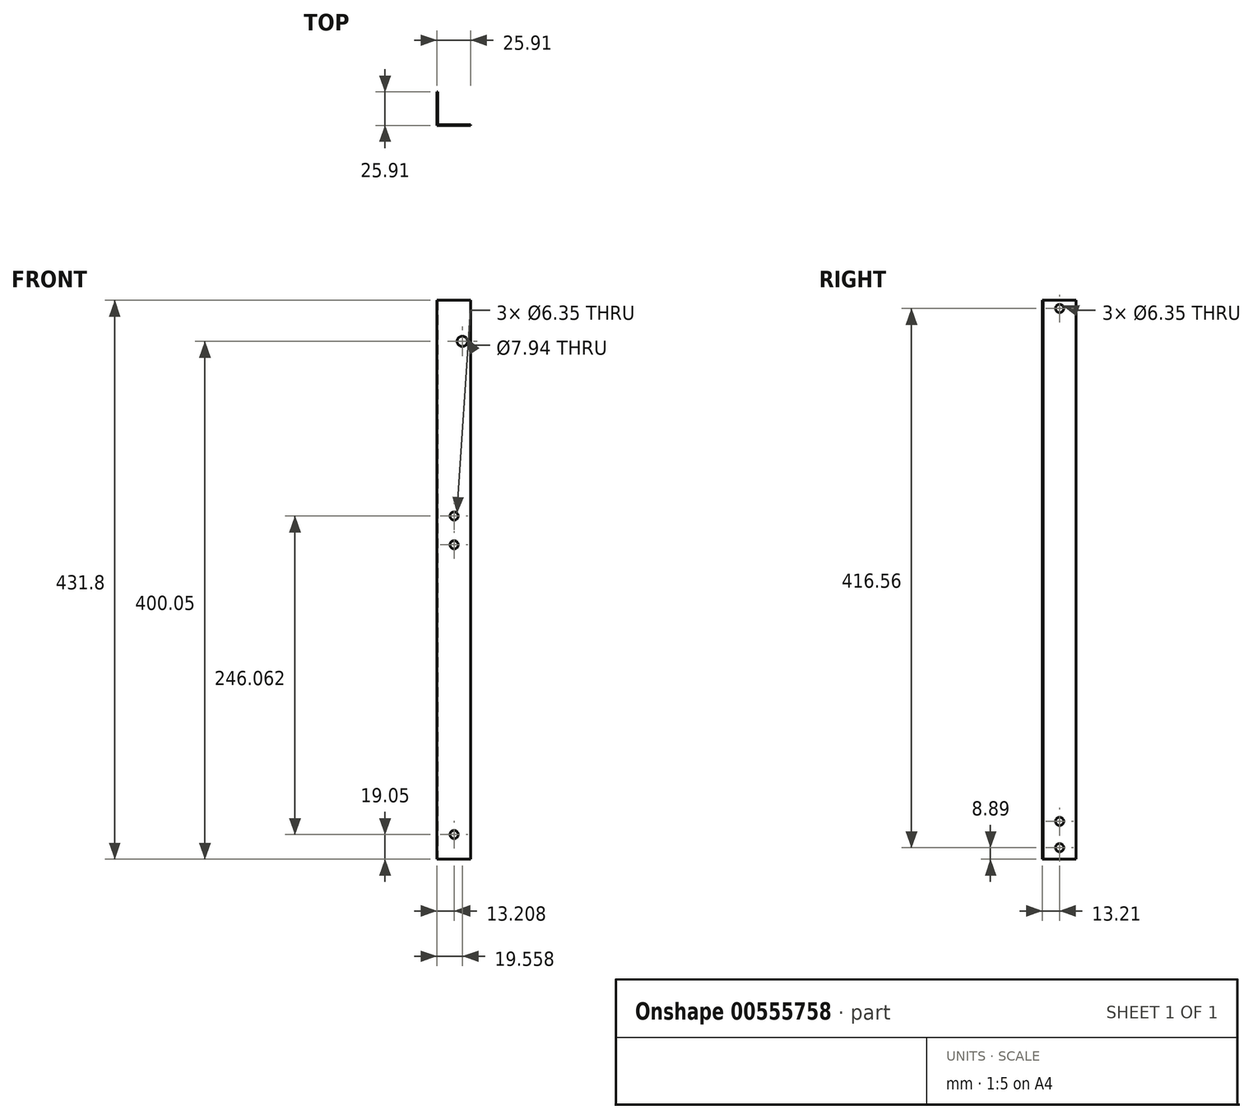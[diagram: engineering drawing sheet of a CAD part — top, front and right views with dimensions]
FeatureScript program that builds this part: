
annotation { "Feature Type Name" : "Feature", "Feature Type Description" : "" }
export const myFeature = defineFeature(function(context is Context, id is Id, definition is map)
    precondition{}
    {
        {
            var Q0;
            Q0=qCreatedBy(makeId("Top.planeOp"),FACE);
            var sketch = newSketch(context, id + "F0", { "sketchPlane" : qUnion([Q0])});
            skLineSegment(sketch, "E0.bottom", {"start": v(0, 0) * mm, "end": v(0.5, 0) * mm});
            skLineSegment(sketch, "E0.top", {"start": v(0, -25.9) * mm, "end": v(0.5, -25.9) * mm});
            skLineSegment(sketch, "E0.left", {"start": v(0, 0) * mm, "end": v(0, -25.9) * mm});
            skLineSegment(sketch, "E0.right", {"start": v(0.5, 0) * mm, "end": v(0.5, -25.9) * mm});
            skSolve(sketch);
        }
        {
            var Q0;
            Q0=makeQuery(id+"F0.imprint","IMPRINT",FACE,{"disambiguationData":[TD([[makeQuery(id+"F0.imprint","IMPRINT",EDGE,{"derivedFrom":sQuery(id+"F0.wireOp",EDGE,"E0.bottom")}),-1.0]])]});
            extrude(context, id + "F1", {"entities" : qUnion([Q0]), "depth" : 431.8 * mm, "offsetDistance" : 25.4 * mm});
        }
        {
            var Q0;
            Q0=makeQuery(id+"F1.opExtrude","SWEPT_FACE",FACE,{"disambiguationData":[OSD([sQuery(id+"F0.wireOp",EDGE,"E0.right")])]});
            var sketch = newSketch(context, id + "F2", { "sketchPlane" : qUnion([Q0])});
            skLineSegment(sketch, "E1.bottom", {"start": v(-25.9, 431.8) * mm, "end": v(-25.4, 431.8) * mm});
            skLineSegment(sketch, "E1.top", {"start": v(-25.9, 0) * mm, "end": v(-25.4, 0) * mm});
            skLineSegment(sketch, "E1.left", {"start": v(-25.9, 431.8) * mm, "end": v(-25.9, 0) * mm});
            skLineSegment(sketch, "E1.right", {"start": v(-25.4, 431.8) * mm, "end": v(-25.4, 0) * mm});
            skSolve(sketch);
        }
        {
            var Q0;
            Q0=makeQuery(id+"F2.imprint","IMPRINT",FACE,{"disambiguationData":[TD([[makeQuery(id+"F2.imprint","IMPRINT",EDGE,{"derivedFrom":sQuery(id+"F2.wireOp",EDGE,"E1.bottom")}),1.0]])]});
            extrude(context, id + "F3", {"entities" : qUnion([Q0]), "operationType" : NewBodyOperationType.ADD, "depth" : 25.4 * mm, "offsetDistance" : 25.4 * mm});
        }
        {
            var Q0;
            Q0=makeQuery(id+"F1.opExtrude","SWEPT_FACE",FACE,{"disambiguationData":[OSD([sQuery(id+"F0.wireOp",EDGE,"E0.right")])]});
            var sketch = newSketch(context, id + "F4", { "sketchPlane" : qUnion([Q0])});
            skCircle(sketch, "E2", {"center": v(-12.7, 425.45) * mm, "radius": 3.18 * mm});
            skCircle(sketch, "E3", {"center": v(-12.7, 29.21) * mm, "radius": 3.18 * mm});
            skCircle(sketch, "E4", {"center": v(-12.7, 8.9) * mm, "radius": 3.18 * mm});
            skSolve(sketch);
        }
        {
            var Q0;
            Q0=makeQuery(id+"F4.imprint","IMPRINT",FACE,{"disambiguationData":[TD([[makeQuery(id+"F4.imprint","IMPRINT",EDGE,{"derivedFrom":sQuery(id+"F4.wireOp",EDGE,"E2")}),1.0]])]});
            var Q1;
            Q1=makeQuery(id+"F4.imprint","IMPRINT",FACE,{"disambiguationData":[TD([[makeQuery(id+"F4.imprint","IMPRINT",EDGE,{"derivedFrom":sQuery(id+"F4.wireOp",EDGE,"E3")}),1.0]])]});
            var Q2;
            Q2=makeQuery(id+"F4.imprint","IMPRINT",FACE,{"disambiguationData":[TD([[makeQuery(id+"F4.imprint","IMPRINT",EDGE,{"derivedFrom":sQuery(id+"F4.wireOp",EDGE,"E4")}),1.0]])]});
            extrude(context, id + "F5", {"entities" : qUnion([Q0, Q1, Q2]), "operationType" : NewBodyOperationType.REMOVE, "oppositeDirection" : true, "depth" : 25.4 * mm, "offsetDistance" : 25.4 * mm});
        }
        {
            var Q0;
            Q0=makeQuery(id+"F3.opExtrude","SWEPT_FACE",FACE,{"disambiguationData":[OSD([sQuery(id+"F2.wireOp",EDGE,"E1.right")])]});
            var sketch = newSketch(context, id + "F6", { "sketchPlane" : qUnion([Q0])});
            skCircle(sketch, "E5", {"center": v(-19.56, 400.05) * mm, "radius": 3.97 * mm});
            skCircle(sketch, "E6", {"center": v(-13.2, 242.89) * mm, "radius": 3.18 * mm});
            skCircle(sketch, "E7", {"center": v(-13.2, 265.11) * mm, "radius": 3.18 * mm});
            skLineSegment(sketch, "E8", {"start": v(-13.2, 265.11) * mm, "end": v(-13.2, 242.89) * mm, "construction": true});
            skPoint(sketch, "E9", {"position": v(-13.2, 254) * mm});
            skCircle(sketch, "E10", {"center": v(-13.2, 19.05) * mm, "radius": 3.18 * mm});
            skSolve(sketch);
        }
        {
            var Q0;
            Q0=makeQuery(id+"F6.imprint","IMPRINT",FACE,{"disambiguationData":[TD([[makeQuery(id+"F6.imprint","IMPRINT",EDGE,{"derivedFrom":sQuery(id+"F6.wireOp",EDGE,"E5")}),1.0]])]});
            var Q1;
            Q1=makeQuery(id+"F6.imprint","IMPRINT",FACE,{"disambiguationData":[TD([[makeQuery(id+"F6.imprint","IMPRINT",EDGE,{"derivedFrom":sQuery(id+"F6.wireOp",EDGE,"E7")}),1.0]])]});
            var Q2;
            Q2=makeQuery(id+"F6.imprint","IMPRINT",FACE,{"disambiguationData":[TD([[makeQuery(id+"F6.imprint","IMPRINT",EDGE,{"derivedFrom":sQuery(id+"F6.wireOp",EDGE,"E6")}),1.0]])]});
            var Q3;
            Q3=makeQuery(id+"F6.imprint","IMPRINT",FACE,{"disambiguationData":[TD([[makeQuery(id+"F6.imprint","IMPRINT",EDGE,{"derivedFrom":sQuery(id+"F6.wireOp",EDGE,"E10")}),1.0]])]});
            extrude(context, id + "F7", {"entities" : qUnion([Q0, Q1, Q2, Q3]), "operationType" : NewBodyOperationType.REMOVE, "oppositeDirection" : true, "depth" : 25.4 * mm, "offsetDistance" : 25.4 * mm});
        }
    });
